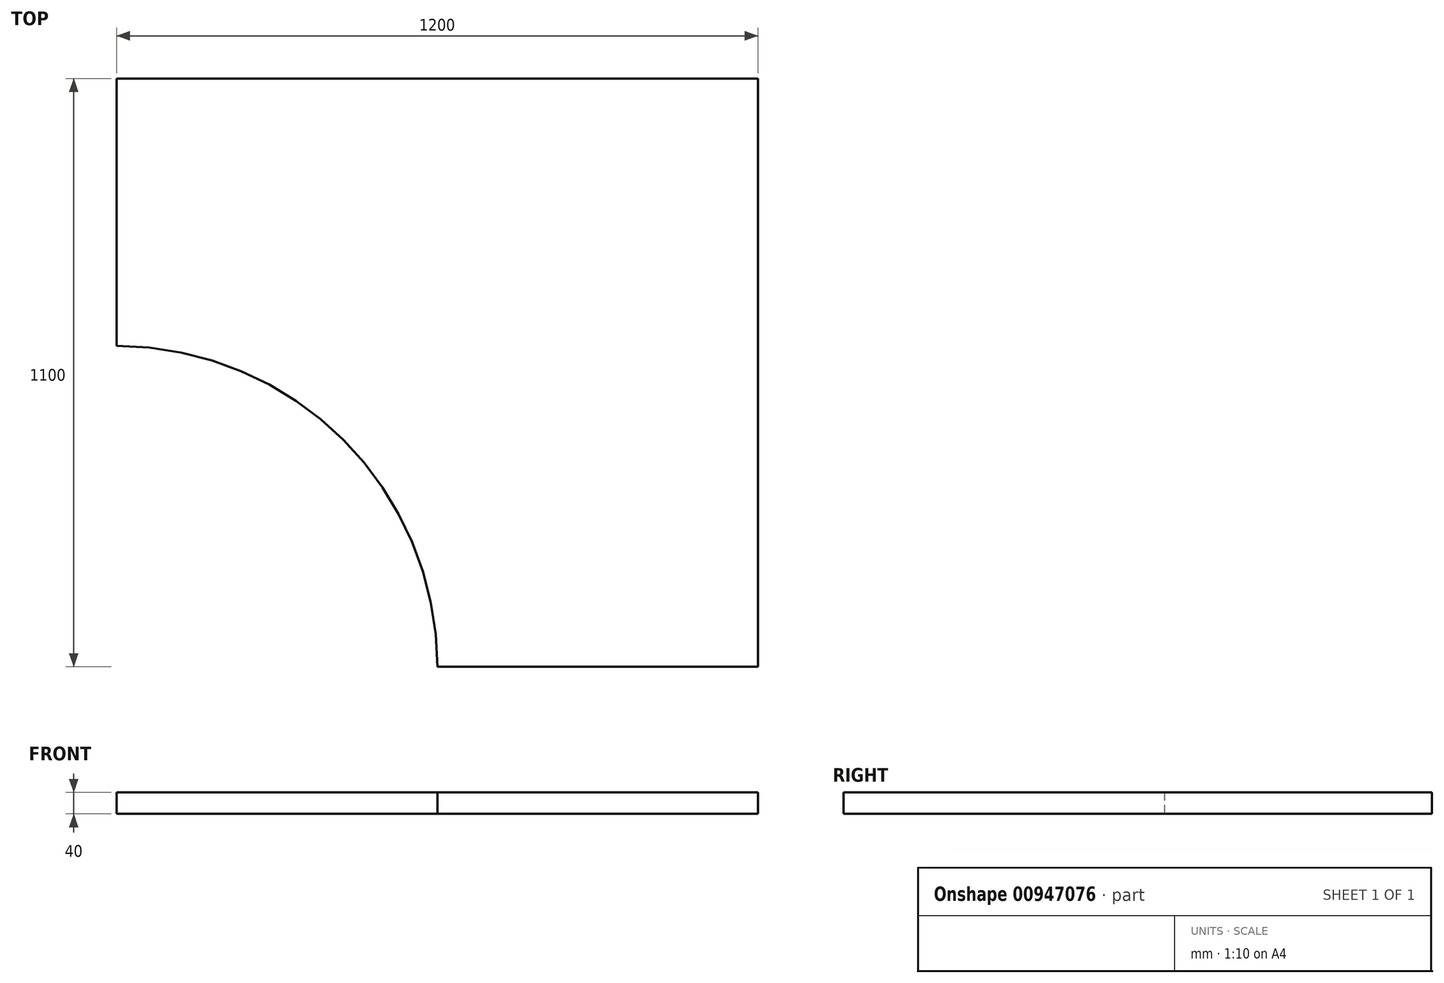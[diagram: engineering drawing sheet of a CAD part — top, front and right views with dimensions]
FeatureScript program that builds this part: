
annotation { "Feature Type Name" : "Feature", "Feature Type Description" : "" }
export const myFeature = defineFeature(function(context is Context, id is Id, definition is map)
    precondition{}
    {
        {
            var Q0;
            Q0=qCreatedBy(makeId("Top.planeOp"),FACE);
            var sketch = newSketch(context, id + "F0", { "sketchPlane" : qUnion([Q0])});
            skLineSegment(sketch, "E0.bottom", {"start": v(600, -600) * mm, "end": v(-600, -600) * mm});
            skLineSegment(sketch, "E0.top", {"start": v(600, 600) * mm, "end": v(-600, 600) * mm});
            skLineSegment(sketch, "E0.left", {"start": v(600, -600) * mm, "end": v(600, 600) * mm});
            skLineSegment(sketch, "E0.right", {"start": v(-600, -600) * mm, "end": v(-600, 600) * mm});
            skPoint(sketch, "E0.middle", {"position": v(0, 0) * mm});
            skPoint(sketch, "E1", {"position": v(-600, 0) * mm});
            skPoint(sketch, "E2", {"position": v(0, -600) * mm});
            skCircle(sketch, "E3", {"center": v(-600, -600) * mm, "radius": 600 * mm});
            skLineSegment(sketch, "E4", {"start": v(-600, 500) * mm, "end": v(600, 500) * mm});
            skSolve(sketch);
        }
        {
            var Q0;
            {var subQ0=sQuery(id+"F0.wireOp",EDGE,"E4");Q0=makeQuery(id+"F0.imprint","IMPRINT",FACE,{"disambiguationData":[TD([[makeQuery(id+"F0.imprint","IMPRINT",EDGE,{"derivedFrom":subQ0}),-1.0]])]});}
            extrude(context, id + "F1", {"entities" : qUnion([Q0]), "depth" : 40 * mm, "offsetDistance" : 25 * mm});
        }
    });
